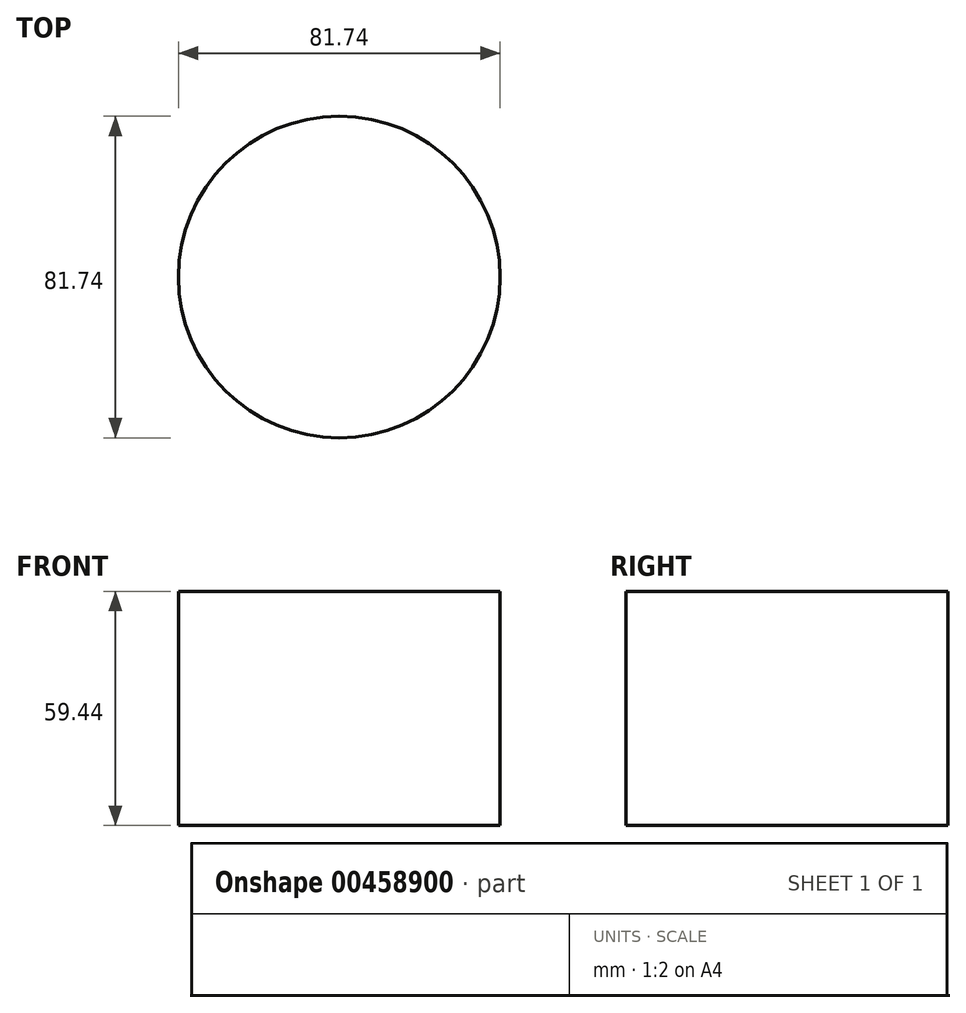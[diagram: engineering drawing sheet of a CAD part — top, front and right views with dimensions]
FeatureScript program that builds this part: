
annotation { "Feature Type Name" : "Feature", "Feature Type Description" : "" }
export const myFeature = defineFeature(function(context is Context, id is Id, definition is map)
    precondition{}
    {
        {
            var Q0;
            Q0=qCreatedBy(makeId("Top.planeOp"),FACE);
            var sketch = newSketch(context, id + "F0", { "sketchPlane" : qUnion([Q0])});
            skCircle(sketch, "E0", {"center": v(0, 0) * mm, "radius": 40.87 * mm});
            skSolve(sketch);
        }
        {
            var Q0;
            Q0 = qSketchRegion(id + "F0", true);
            extrude(context, id + "F1", {"entities" : qUnion([Q0]), "depth" : 59.44 * mm});
        }
    });
